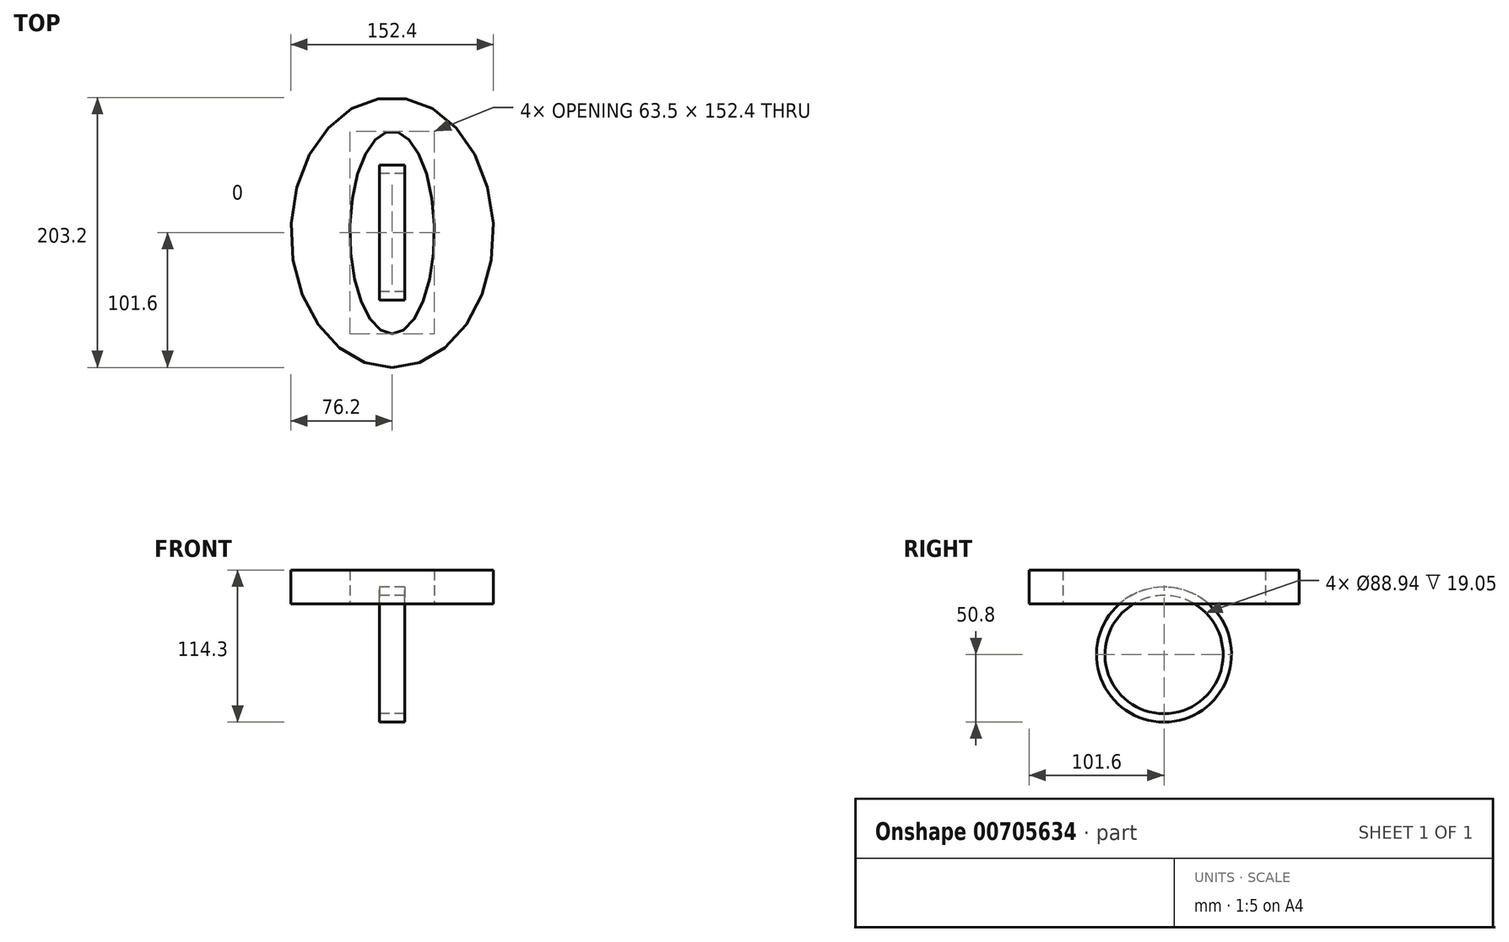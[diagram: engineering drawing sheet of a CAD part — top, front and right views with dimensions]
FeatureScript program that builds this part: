
annotation { "Feature Type Name" : "Feature", "Feature Type Description" : "" }
export const myFeature = defineFeature(function(context is Context, id is Id, definition is map)
    precondition{}
    {
        {
            var Q0;
            Q0=qCreatedBy(makeId("Top.planeOp"),FACE);
            var sketch = newSketch(context, id + "F0", { "sketchPlane" : qUnion([Q0])});
            skEllipse(sketch, "E0", {"center": v(0, 0) * mm, "majorRadius": 101.6 * mm, "minorRadius": 76.2 * mm, "majorAxis": v(0, -1)});
            skLineSegment(sketch, "E1", {"start": v(-76.2, 0) * mm, "end": v(76.2, 0) * mm, "construction": true});
            skEllipse(sketch, "E2", {"center": v(0, 0) * mm, "majorRadius": 76.2 * mm, "minorRadius": 31.75 * mm, "majorAxis": v(0, -1)});
            skSolve(sketch);
        }
        {
            var Q0;
            Q0 = qSketchRegion(id + "F0", true);
            extrude(context, id + "F1", {"entities" : qUnion([Q0]), "endBound" : BoundingType.SYMMETRIC, "depth" : 25.4 * mm, "offsetDistance" : 25.4 * mm});
        }
        {
            var Q0;
            Q0=qCreatedBy(makeId("Right.planeOp"),FACE);
            var sketch = newSketch(context, id + "F2", { "sketchPlane" : qUnion([Q0])});
            skCircle(sketch, "E3", {"center": v(0, -50.8) * mm, "radius": 50.8 * mm});
            skCircle(sketch, "E4", {"center": v(0, -50.8) * mm, "radius": 44.47 * mm});
            skSolve(sketch);
        }
        {
            var Q0;
            Q0=makeQuery(id+"F2.imprint","IMPRINT",FACE,{"disambiguationData":[TD([[makeQuery(id+"F2.imprint","IMPRINT",EDGE,{"derivedFrom":sQuery(id+"F2.wireOp",EDGE,"E3")}),1.0]])]});
            extrude(context, id + "F3", {"entities" : qUnion([Q0]), "endBound" : BoundingType.SYMMETRIC, "depth" : 19.05 * mm, "offsetDistance" : 25.4 * mm});
        }
    });
